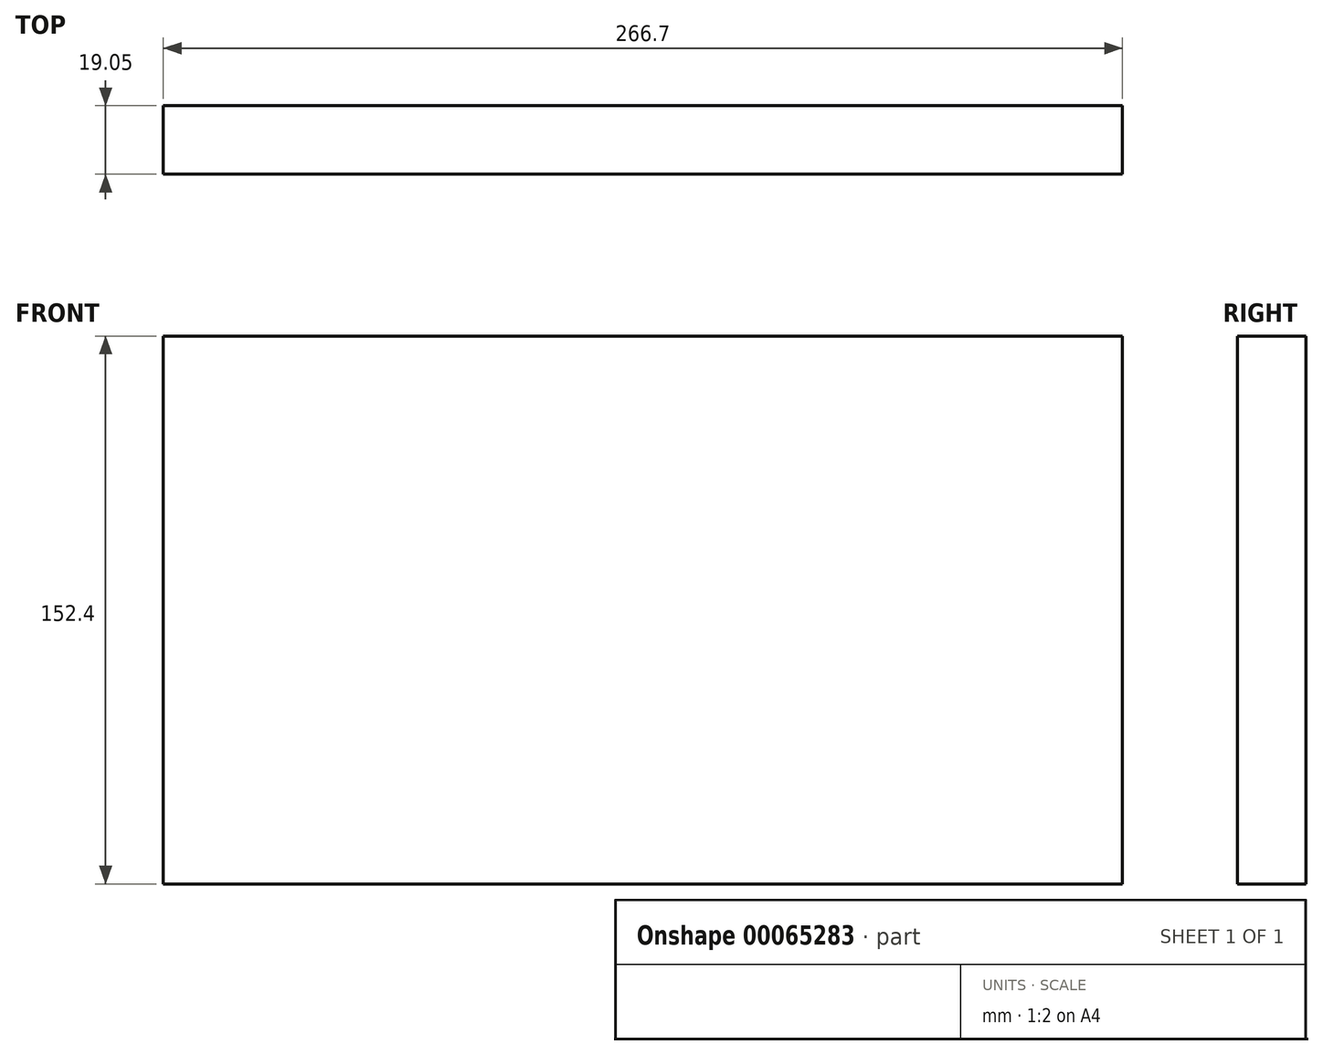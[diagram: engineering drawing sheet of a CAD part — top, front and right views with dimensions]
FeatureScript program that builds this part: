
annotation { "Feature Type Name" : "Feature", "Feature Type Description" : "" }
export const myFeature = defineFeature(function(context is Context, id is Id, definition is map)
    precondition{}
    {
        {
            var Q0;
            Q0=qCreatedBy(makeId("Front.planeOp"),FACE);
            var sketch = newSketch(context, id + "F0", { "sketchPlane" : qUnion([Q0])});
            skLineSegment(sketch, "E0.bottom", {"start": v(-67.57, 83.22) * mm, "end": v(199.13, 83.22) * mm});
            skLineSegment(sketch, "E0.top", {"start": v(-67.57, -69.18) * mm, "end": v(199.13, -69.18) * mm});
            skLineSegment(sketch, "E0.left", {"start": v(-67.57, 83.22) * mm, "end": v(-67.57, -69.18) * mm});
            skLineSegment(sketch, "E0.right", {"start": v(199.13, 83.22) * mm, "end": v(199.13, -69.18) * mm});
            skSolve(sketch);
        }
        {
            var Q0;
            Q0=makeQuery(id+"F0.imprint","IMPRINT",FACE,{"disambiguationData":[TD([[makeQuery(id+"F0.imprint","IMPRINT",EDGE,{"derivedFrom":sQuery(id+"F0.wireOp",EDGE,"E0.bottom")}),-1.0]])]});
            extrude(context, id + "F1", {"entities" : qUnion([Q0]), "depth" : 19.05 * mm});
        }
    });
